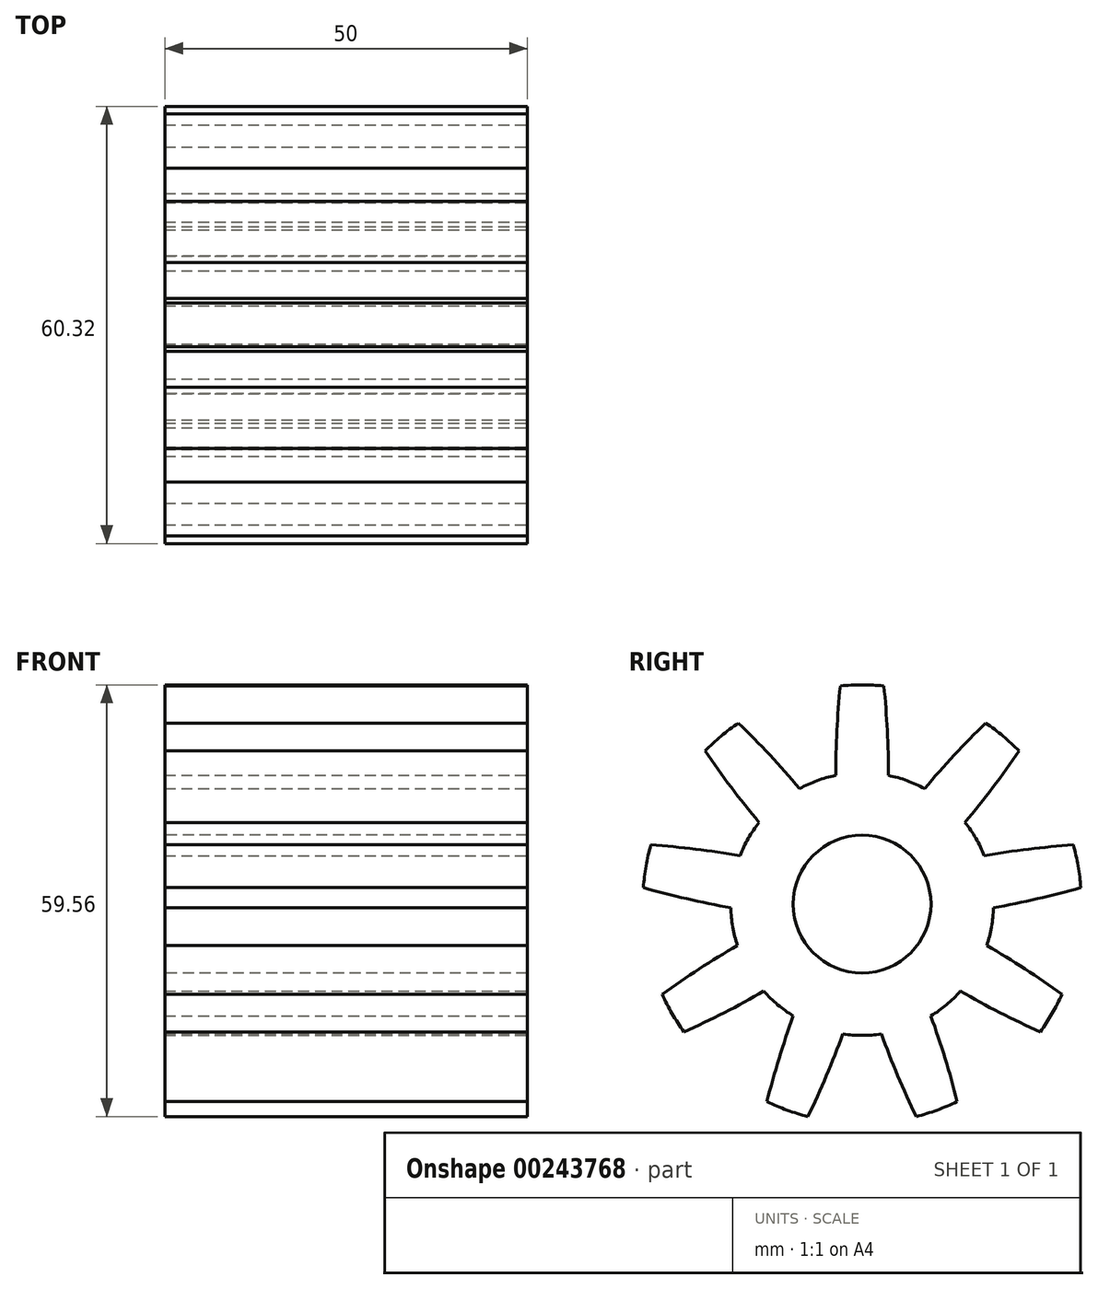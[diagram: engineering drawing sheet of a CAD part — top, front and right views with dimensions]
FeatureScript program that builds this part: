
annotation { "Feature Type Name" : "Feature", "Feature Type Description" : "" }
export const myFeature = defineFeature(function(context is Context, id is Id, definition is map)
    precondition{}
    {
        {
            var Q0;
            Q0=qCreatedBy(makeId("Front.planeOp"),FACE);
            var sketch = newSketch(context, id + "F0", { "sketchPlane" : qUnion([Q0])});
            skLineSegment(sketch, "E0.bottom", {"start": v(-50, 30.25) * mm, "end": v(0, 30.25) * mm});
            skLineSegment(sketch, "E0.top", {"start": v(-50, 9.5) * mm, "end": v(0, 9.5) * mm});
            skLineSegment(sketch, "E0.left", {"start": v(-50, 30.25) * mm, "end": v(-50, 9.5) * mm});
            skLineSegment(sketch, "E0.right", {"start": v(0, 30.25) * mm, "end": v(0, 9.5) * mm});
            skLineSegment(sketch, "E1", {"start": v(-55.21, 0) * mm, "end": v(15.07, 0) * mm, "construction": true});
            skSolve(sketch);
        }
        {
            var Q0;
            Q0=makeQuery(id+"F0.imprint","IMPRINT",FACE,{"disambiguationData":[TD([[makeQuery(id+"F0.imprint","IMPRINT",EDGE,{"derivedFrom":sQuery(id+"F0.wireOp",EDGE,"E0.bottom")}),-1.0]])]});
            var Q1;
            Q1=sQuery(id+"F0.wireOp",EDGE,"E1");
            revolve(context, id + "F1", {"entities" : qUnion([Q0]), "axis" : qUnion([Q1]), "revolveType" : RevolveType.FULL});
        }
        {
            var Q0;
            Q0=makeQuery(id+"F1.opRevolve","SWEPT_FACE",FACE,{"disambiguationData":[OSD([sQuery(id+"F0.wireOp",EDGE,"E0.right")])]});
            var sketch = newSketch(context, id + "F2", { "sketchPlane" : qUnion([Q0])});
            skLineSegment(sketch, "E2", {"start": v(0, 0) * mm, "end": v(0, 38.44) * mm, "construction": true});
            skArc(sketch, "E3", {"start": v(-3.64, 17.75) * mm, "mid": v(-6.2, 17.03) * mm, "end": v(-8.62, 15.94) * mm});
            skLineSegment(sketch, "E4", {"start": v(0, 0) * mm, "end": v(-6.42, 36.44) * mm, "construction": true});
            skLineSegment(sketch, "E5", {"start": v(0, 0) * mm, "end": v(-11.96, 32.87) * mm, "construction": true});
            skArc(sketch, "E6", {"start": v(-3, 30.1) * mm, "mid": v(-3.48, 23.93) * mm, "end": v(-3.64, 17.75) * mm});
            skArc(sketch, "E7.MirrorCS", {"start": v(-17.05, 24.99) * mm, "mid": v(-12.72, 20.57) * mm, "end": v(-8.62, 15.94) * mm});
            skArc(sketch, "E8", {"start": v(-3, 30.1) * mm, "mid": v(-10.35, 28.43) * mm, "end": v(-17.05, 24.99) * mm});
            skSolve(sketch);
        }
        {
            var Q0;
            Q0=qSketchRegion(id+"F2",true);
            extrude(context, id + "F3", {"entities" : qUnion([Q0]), "operationType" : NewBodyOperationType.REMOVE, "endBound" : BoundingType.THROUGH_ALL, "oppositeDirection" : true, "depth" : 25 * mm});
        }
        {
            var Q0;
            Q0=makeQuery(id+"F3.boolean.opBoolean","COPY",FACE,{"derivedFrom":makeQuery(id+"F3.opExtrude","SWEPT_FACE",FACE,{"disambiguationData":[OSD([sQuery(id+"F2.wireOp",EDGE,"E6")])]})});
            var Q1;
            Q1=makeQuery(id+"F3.boolean.opBoolean","COPY",FACE,{"derivedFrom":makeQuery(id+"F3.opExtrude","SWEPT_FACE",FACE,{"disambiguationData":[OSD([sQuery(id+"F2.wireOp",EDGE,"E3")])]})});
            var Q2;
            Q2=makeQuery(id+"F3.boolean.opBoolean","COPY",FACE,{"derivedFrom":makeQuery(id+"F3.opExtrude","SWEPT_FACE",FACE,{"disambiguationData":[OSD([sQuery(id+"F2.wireOp",EDGE,"E7.MirrorCS")])]})});
            var Q3;
            Q3=sQuery(id+"F0.wireOp",EDGE,"E1");
            circularPattern(context, id + "F4", {"patternType" : PatternType.FACE, "faces" : qUnion([Q0, Q1, Q2]), "axis" : qUnion([Q3]), "angle" : 360 * degree, "instanceCount" : 9, "equalSpace" : true});
        }
    });
